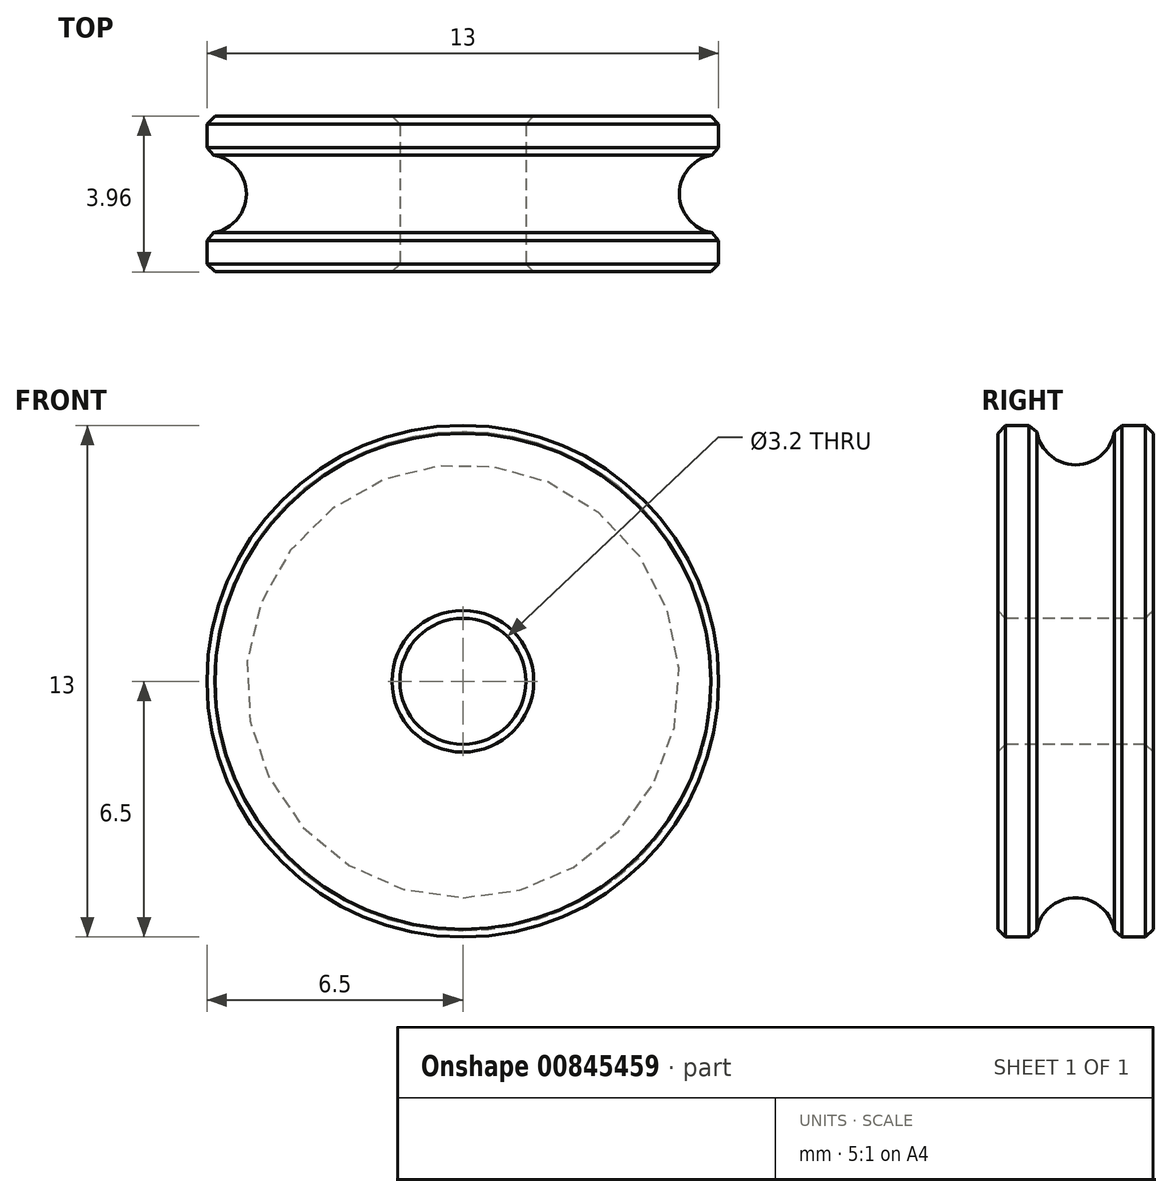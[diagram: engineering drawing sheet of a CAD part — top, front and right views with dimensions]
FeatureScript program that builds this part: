
annotation { "Feature Type Name" : "Feature", "Feature Type Description" : "" }
export const myFeature = defineFeature(function(context is Context, id is Id, definition is map)
    precondition{}
    {
        {
            var Q0;
            Q0=qCreatedBy(makeId("Right.planeOp"),FACE);
            var sketch = newSketch(context, id + "F0", { "sketchPlane" : qUnion([Q0])});
            skLineSegment(sketch, "E0", {"start": v(0, 0) * mm, "end": v(0, 1.6) * mm, "construction": true});
            skLineSegment(sketch, "E1", {"start": v(0, 1.6) * mm, "end": v(-1.98, 1.6) * mm});
            skLineSegment(sketch, "E2", {"start": v(-1.98, 1.6) * mm, "end": v(-1.98, 6.5) * mm});
            skLineSegment(sketch, "E3", {"start": v(-1.98, 6.5) * mm, "end": v(-1, 6.5) * mm});
            skLineSegment(sketch, "E4", {"start": v(-1, 6.5) * mm, "end": v(1, 6.5) * mm, "construction": true});
            skLineSegment(sketch, "E5", {"start": v(1, 6.5) * mm, "end": v(1.98, 6.5) * mm});
            skLineSegment(sketch, "E6", {"start": v(1.98, 6.5) * mm, "end": v(1.98, 1.6) * mm});
            skLineSegment(sketch, "E7", {"start": v(1.98, 1.6) * mm, "end": v(0, 1.6) * mm});
            skArc(sketch, "E8", {"start": v(-1, 6.5) * mm, "mid": v(0, 5.5) * mm, "end": v(1, 6.5) * mm});
            skLineSegment(sketch, "E9", {"start": v(0, 0) * mm, "end": v(5.07, 0) * mm});
            skSolve(sketch);
        }
        {
            var Q0;
            Q0=makeQuery(id+"F0.imprint","IMPRINT",FACE,{"disambiguationData":[TD([[makeQuery(id+"F0.imprint","IMPRINT",EDGE,{"derivedFrom":sQuery(id+"F0.wireOp",EDGE,"E1")}),-1.0]])]});
            var Q1;
            Q1=sQuery(id+"F0.wireOp",EDGE,"E9");
            revolve(context, id + "F1", {"surfaceOperationType" : NewSurfaceOperationType.NEW, "entities" : qUnion([Q0]), "axis" : qUnion([Q1]), "revolveType" : RevolveType.FULL});
        }
        {
            var Q0;
            Q0=makeQuery(id+"F1.opRevolve","SWEPT_FACE",FACE,{"disambiguationData":[OSD([sQuery(id+"F0.wireOp",EDGE,"E1"),sQuery(id+"F0.wireOp",EDGE,"E7")])]});
            var Q1;
            Q1=makeQuery(id+"F1.opRevolve","SWEPT_FACE",FACE,{"disambiguationData":[OSD([sQuery(id+"F0.wireOp",EDGE,"E3")])]});
            var Q2;
            Q2=makeQuery(id+"F1.opRevolve","SWEPT_FACE",FACE,{"disambiguationData":[OSD([sQuery(id+"F0.wireOp",EDGE,"E5")])]});
            chamfer(context, id + "F2", {"entities" : qUnion([Q0, Q1, Q2]), "width" : 0.2 * mm, "tangentPropagation" : true});
        }
    });
